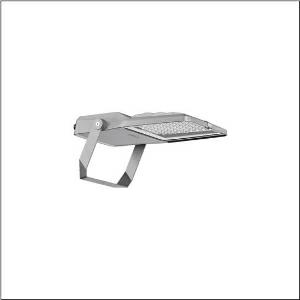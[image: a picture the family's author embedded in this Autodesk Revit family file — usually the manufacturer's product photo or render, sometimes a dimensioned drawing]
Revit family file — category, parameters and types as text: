
# Revit family: floodlight_fl_21_iq_mini___pl52_5xa7772c5d1a_6522
name_source: partatom
category: Lighting Fixtures
units: mm (PartAtom-declared; Revit-internal decimal feet)

## family parameters
Cut with Voids When Loaded = No
Host = Face
Light Source = No
Part Type = Normal
Room Calculation Point = No
Round Connector Dimension = Use Diameter
Shared = No

## types (1)
- --- (1 x LED, 11390 lm, 87.2 W, 4000K)
    Apparent Load = 87 VA
    CIE Flux Codes = 26 60 98 100 100
    Color Rendering = 80
    Color Temperature = 4000K
    Default Elevation = 1800 mm
    Description = Floodlight FL 21 iQ mini, floodlight, primary light control with lens, of PMMA, primary optical cover: protective disc, of toughened safety glass, transparent, light distribution: PL52, light emission: direct distribution, installation type: surface-mounted, LED, High Power LED, rated luminous flux: 11.390lm, luminous efficacy: 131lm/W, light colour: 840, colour temperature: 4000K, control gear: iQ Street-Remote/DALI, control: Street-Remote, Auto-Match, Temp-Guard, Night-Set, Smart-Wire, Desk-Remote (wireless, voltage-free reading and setting of iQ features in the workshop via application-optimized NFC function/RFID function), optimised constant luminous flux control (CLO 2.0), with terminal, 6-pole, mains connection: 220..240V, AC, 50/60Hz, start of lifetime: 87W, end of service life: 92W, reduction: 40W, luminaire housing, of diecast aluminium, powder-coated, Siteco® metallic grey (DB 702S), corrosivity category C5 mid according to DIN EN ISO 12944, suitable for swimming pools, chlorine-resistant, sealing non-destructively replaceable, mounting bracket, of steel, galvanised, powder-coated, Siteco® metallic grey (DB 702S), protection rating (complete): IP66, insulation class (complete): insulation class II (safety insulation), certification: CE, ENEC, VDE, protection symbol: D, impact resistance: IK08, permissible operating ambient temperature: -40..+40°C, permissible operating ambient temperature for outdoor applications: -40..+50°C, standard: DIN EN 12944, LABS conformity tested according to VDMA 24364:2018-05, packaging unit: 1 piece

Light Distribution: PL52
    Height = 70 mm
    Lamp = 1 x LED
    Lamp Light Flux = 11390 lm
    Lamp Power = 87.2 W
    Lamp count = 1
    Length = 485 mm
    Luminous efficacy = 131 lm/W
    Manufacturer = Siteco
    ModVariant = No
    Model = 5XA7772C5D1A
    Number of Poles = 1
    OnlyDefault = Yes
    Power Factor = 1
    Product Name = Floodlight FL 21 iQ mini | PL52
    Product group = floodlight | pylon annexe
    ProductGroupID = 6200
    Protection Class = Protection class II
    Protection Degree = IP 66
    RLX_Detail_Level = 1
    RLX_Emergency_Light_Flux = 0 lm
    RLX_Emergency_Type = 0
    RLX_Emergency_Type_DB = No
    RlxData = <blob elided: 96517 chars, md5=ea13fc06>
    Socket = socket
    Standby Power = 0 W
    System Light Flux = 11390 lm
    System Power = 87 W
    Type Comments = factory setting: luminous flux: 100 % | dim-lin: 254 | 456 mA
    Type Image = l_1006845.jpg
    URL = http://relux.com
    VarID = @adj_164124
    Voltage = 0 V
    Weight = 0.00 kg
    Width = 337 mm

## geometry (parser evidence)
native form markers: Blend x4, Sweep x11
no freeform markers — native parametric forms only
